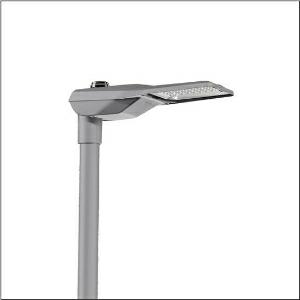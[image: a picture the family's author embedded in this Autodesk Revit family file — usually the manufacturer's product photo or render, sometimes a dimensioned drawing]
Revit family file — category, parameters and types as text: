
# Revit family: streetlight_sl_21_mini___p1_0a_5xe6a47n08gb_c068
name_source: partatom
category: Lighting Fixtures
units: mm (PartAtom-declared; Revit-internal decimal feet)

## family parameters
Cut with Voids When Loaded = No
Host = Face
Light Source = No
Part Type = Normal
Room Calculation Point = No
Round Connector Dimension = Use Diameter
Shared = No

## types (1)
- --- (1 x LED, 6180 lm, 40.4 W, 4000K)
    Apparent Load = 40 VA
    CIE Flux Codes = 21 50 90 100 100
    Color Rendering = 70
    Color Temperature = 4000K
    Default Elevation = 1800 mm
    Description = Streetlight SL 21 mini, mast luminaire, primary light control with lens, of PMMA, primary optical cover: cover, of toughened safety glass, transparent, light distribution: P1.0a, light emission: direct distribution, primary light characteristic: asymmetric, installation type: side-entry, LED, 3G 1.5mm², High Power LED, rated luminous flux: 6.180lm, luminous efficacy: 153lm/W, light colour: 740, colour temperature: 4000K, control gear: NEMA (7pin), control: overheat protection, pre-setting: linear dimming characteristic, constant luminous flux control, time-dependent luminous flux control, flexible luminous flux parameterisation, mains connection: 230..240V, AC, 50/60Hz, connection cable pre-assembled, cable length: 8,5m, wiring characteristics: H07RN-F, start of lifetime: 40W, end of service life: 41W, reduction: 19W, luminaire housing, of diecast aluminium (EN AC-44300), powder-coated, Siteco® metallic grey (DB 702S), corrosivity category C5 mid according to DIN EN ISO 12944, multi-level sealing system, sealing non-destructively replaceable, inclination adjustable: 0°, 5°, 10°, 15°, length: 628mm, width: 235mm, height: 110mm, spigot size: 42mm (side-entry), mounting height: 4..8m, protection rating (complete): IP66, insulation class (complete): insulation class I (protective earthing), certification: CE, ENEC, ENEC+, VDE, impact resistance: IK10, permissible operating ambient temperature for outdoor applications: -40..+50°C, standard-compliant lighting for roads and squares, packaging unit: 1 piece

Light Distribution: P1.0a
    Height = 110 mm
    Lamp = 1 x LED
    Lamp Light Flux = 6180 lm
    Lamp Power = 40.4 W
    Lamp count = 1
    Length = 625 mm
    Luminous efficacy = 153 lm/W
    Manufacturer = Siteco
    ModVariant = No
    Model = 5XE6A47N08GB
    Number of Poles = 1
    OnlyDefault = Yes
    Power Factor = 1
    Product Name = Streetlight SL 21 mini | P1.0a
    Product group = mast luminaire | pylon top
    ProductGroupID = 6100
    Protection Class = Protection class I
    Protection Degree = IP 66
    RLX_Detail_Level = 1
    RLX_Emergency_Light_Flux = 0 lm
    RLX_Emergency_Type = 0
    RLX_Emergency_Type_DB = No
    RlxData = <blob elided: 37033 chars, md5=9a67d2f3>
    Socket = socket
    Standby Power = 0 W
    System Light Flux = 6180 lm
    System Power = 40 W
    Type Comments = factory setting: luminous flux: 100 % | dim-lin: 254 | 812 mA
    Type Image = l_1294379.jpg
    URL = http://relux.com
    VarID = @adj_134640
    Voltage = 0 V
    Weight = 0.00 kg
    Width = 234 mm

## geometry (parser evidence)
native form markers: Blend x4, Sweep x8
no freeform markers — native parametric forms only
